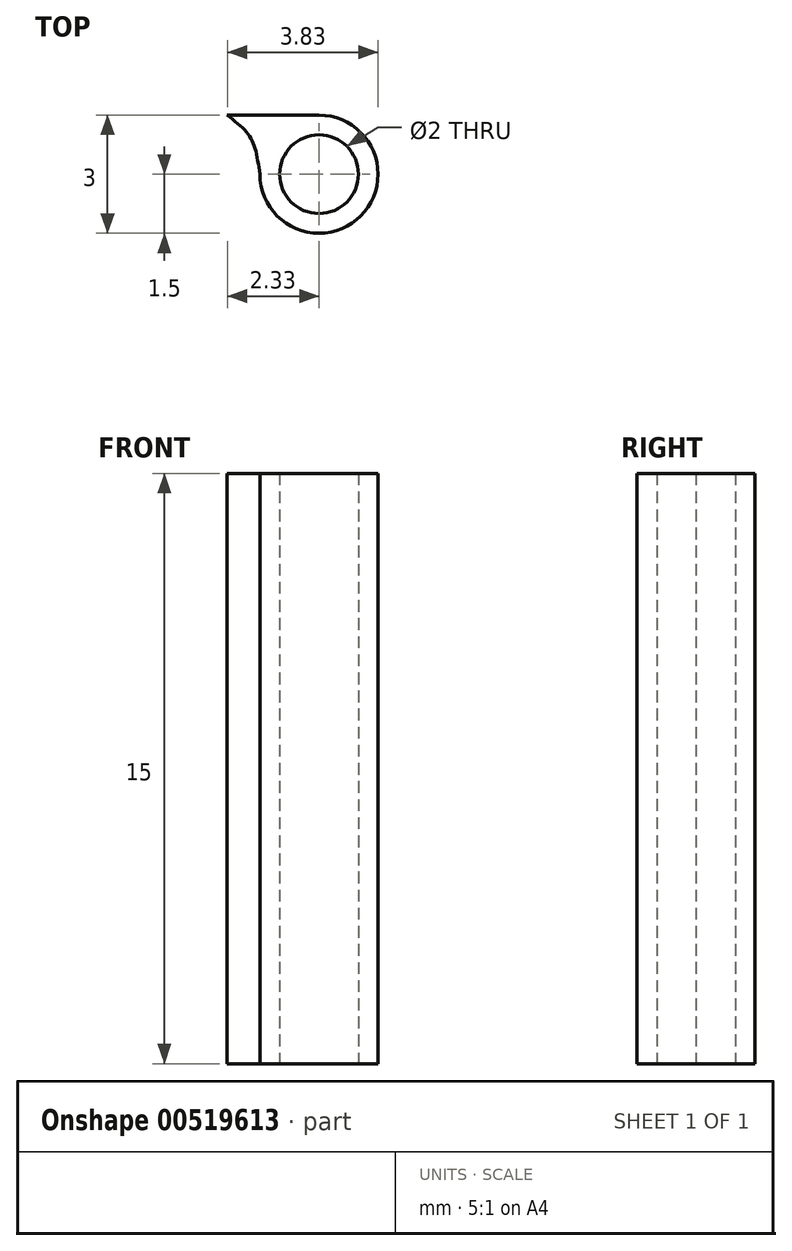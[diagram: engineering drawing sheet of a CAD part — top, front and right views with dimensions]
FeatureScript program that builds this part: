
annotation { "Feature Type Name" : "Feature", "Feature Type Description" : "" }
export const myFeature = defineFeature(function(context is Context, id is Id, definition is map)
    precondition{}
    {
        {
            var Q0;
            Q0=qCreatedBy(makeId("Top.planeOp"),FACE);
            var sketch = newSketch(context, id + "F0", { "sketchPlane" : qUnion([Q0])});
            skCircle(sketch, "E0", {"center": v(0, 0) * mm, "radius": 1 * mm});
            skArc(sketch, "E1", {"start": v(-1.5, 0) * mm, "mid": v(1.06, -1.06) * mm, "end": v(0, 1.5) * mm});
            skLineSegment(sketch, "E2", {"start": v(0, 1.5) * mm, "end": v(-2.33, 1.5) * mm});
            skFitSpline(sketch, "E3", {"points": [v(-2.33, 1.5) * mm, v(-1.84, 1.07) * mm, v(-1.63, 0.67) * mm, v(-1.5, 0) * mm], "startDerivative": vector(1.57, -1.23) * mm, "endDerivative": vector(0.3, -2) * mm});
            skSolve(sketch);
        }
        {
            var Q0;
            Q0 = qSketchRegion(id + "F0", true);
            extrude(context, id + "F1", {"entities" : qUnion([Q0]), "depth" : 15 * mm, "offsetDistance" : 25 * mm});
        }
    });
